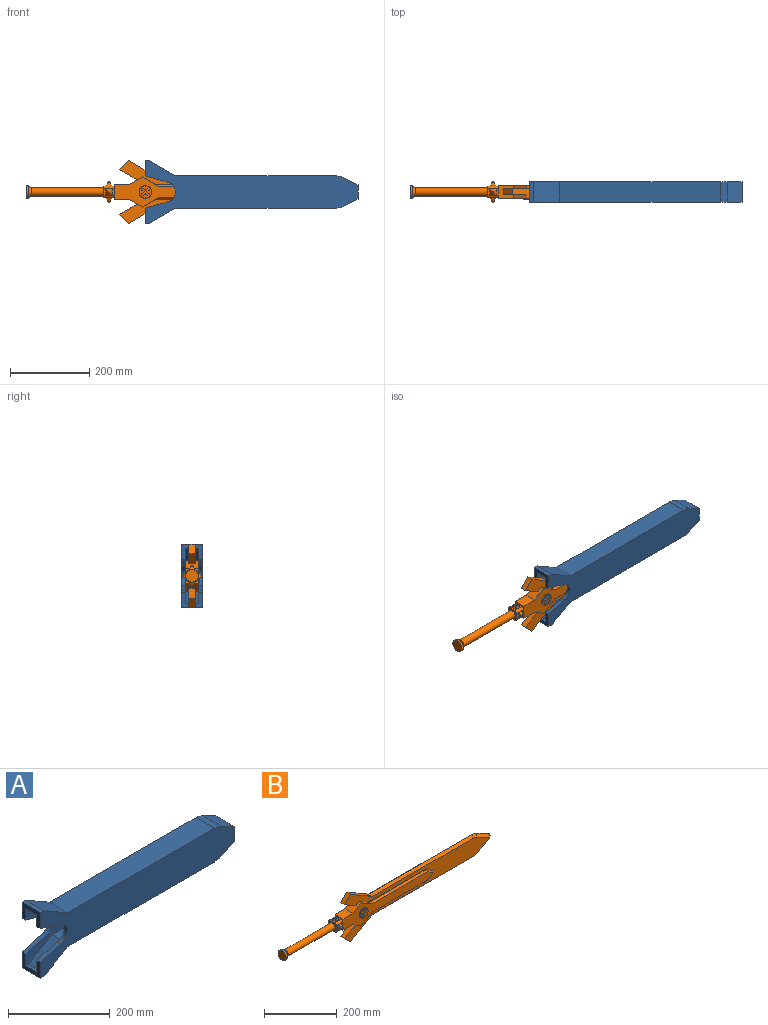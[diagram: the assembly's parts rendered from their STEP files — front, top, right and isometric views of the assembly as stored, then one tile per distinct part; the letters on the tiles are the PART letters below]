
ASSEMBLY  parts=2 mates=1
PART A: 34 faces, bbox 537.1x50.8x157.5 mm
  f0: plane 50.8x38.1mm, normal (-1,0,0), area 1083.9mm2, adj f1,f9,f10,f19,f20,f23,f32,f33
  f1: plane 57.66x16.19mm, normal (-0.27,0,0.96), area 608.5mm2, adj f0,f2,f20,f33
  f2: cylinder r=25.4mm len=48.91mm, axis (0,1,0), area 669.5mm2, adj f1,f3,f20,f33
  f3: plane 57.66x16.19mm, normal (-0.27,0,-0.96), area 608.5mm2, adj f2,f4,f20,f33
  f4: plane 50.8x38.1mm, normal (-1,0,0), area 1083.9mm2, adj f3,f6,f7,f19,f20,f22,f32,f33
  f5: plane 65.99x50.8mm, normal (0.5,0,0.87), area 3871mm2, adj f6,f18,f19,f20
  f6: plane 50.8x10.21mm, normal (0,0,1), area 518.6mm2, adj f4,f5,f19,f20
  f7: plane 57.66x16.19mm, normal (-0.27,0,-0.96), area 608.5mm2, adj f4,f8,f19,f32
  f8: cylinder r=25.4mm len=48.91mm, axis (0,1,0), area 669.5mm2, adj f7,f9,f19,f32
  f9: plane 57.66x16.19mm, normal (-0.27,0,0.96), area 608.5mm2, adj f0,f8,f19,f32
  f10: plane 50.8x10.21mm, normal (0,0,-1), area 518.6mm2, adj f0,f11,f19,f20
  f11: plane 65.99x50.8mm, normal (0.5,0,-0.87), area 3871mm2, adj f10,f12,f19,f20
  f12: plane 406.4x50.8mm, normal (0,0,-1), area 20645.1mm2, adj f11,f13,f19,f20
  f13: cylinder r=40.64mm len=50.8mm, axis (0,1,0), area 957.2mm2, adj f12,f14,f19,f20
  f14: plane 50.8x36.35mm, normal (0.45,0,-0.89), area 2064.5mm2, adj f13,f15,f19,f20
  f15: plane 50.8x36.35mm, normal (1,0,0), area 1846.6mm2, adj f14,f16,f19,f20
  f16: plane 50.8x36.35mm, normal (0.45,0,0.89), area 2064.5mm2, adj f15,f17,f19,f20
  f17: cylinder r=40.64mm len=50.8mm, axis (0,1,0), area 957.2mm2, adj f16,f18,f19,f20
  f18: plane 406.4x50.8mm, normal (0,0,1), area 20645.1mm2, adj f5,f17,f19,f20
  f19: plane 537.12x157.48mm, normal (0,-1,0), area 41503.6mm2, adj f0,f4,f5,f6,f7,f8,f9,f10
  f20: plane 537.12x157.48mm, normal (0,1,0), area 41503.6mm2, adj f0,f1,f2,f3,f4,f5,f6,f10
  f21: plane 65.99x38.1mm, normal (-0.5,0,-0.87), area 2322.6mm2, adj f22,f31,f32,f33
  f22: plane 30.48x7.49mm, normal (0,0,-1), area 228.2mm2, adj f4,f21,f32,f33
  f23: plane 30.48x7.49mm, normal (0,0,1), area 228.2mm2, adj f0,f24,f32,f33
  f24: plane 65.99x38.1mm, normal (-0.5,0,0.87), area 2322.6mm2, adj f23,f25,f32,f33
  f25: plane 409.12x30.48mm, normal (0,0,1), area 12470mm2, adj f24,f26,f32,f33
  f26: cylinder r=30.48mm len=30.48mm, axis (0,1,0), area 430.7mm2, adj f25,f27,f32,f33
  f27: plane 30.73x30.48mm, normal (-0.45,0,0.89), area 1047.3mm2, adj f26,f28,f32,f33
  f28: plane 30.48x23.79mm, normal (-1,0,0), area 725.2mm2, adj f27,f29,f32,f33
  f29: plane 30.73x30.48mm, normal (-0.45,0,-0.89), area 1047.3mm2, adj f28,f30,f32,f33
  f30: cylinder r=30.48mm len=30.48mm, axis (0,1,0), area 430.7mm2, adj f29,f31,f32,f33
  f31: plane 409.12x30.48mm, normal (0,0,-1), area 12470mm2, adj f21,f30,f32,f33
  f32: plane 526.96x137.16mm, normal (0,1,0), area 30087.2mm2, adj f0,f4,f7,f8,f9,f21,f22,f23
  f33: plane 526.96x137.16mm, normal (0,-1,0), area 30087.2mm2, adj f0,f1,f2,f3,f4,f21,f22,f23
PART B: 132 faces, bbox 810.5x54x159.9 mm
  f0: plane 18.57x12.28mm, normal (0,-1,0), area 81.6mm2, adj f80,f81,f82,f105,f106,f107,f108
  f1: plane 18.57x12.28mm, normal (0,-1,0), area 81.6mm2, adj f80,f87,f88,f90,f91,f92,f93
  f2: plane 18.57x12.28mm, normal (0,-1,0), area 81.6mm2, adj f80,f85,f86,f100,f101,f102,f103
  f3: plane 18.57x12.28mm, normal (0,-1,0), area 81.6mm2, adj f80,f83,f84,f95,f96,f97,f98
  f4: plane 10.7x10.7mm, normal (0,0.89,-0.45), area 64mm2, adj f8,f55,f57
  f5: plane 10.7x10.7mm, normal (0,-0.89,-0.45), area 64mm2, adj f8,f53,f54
  f6: plane 10.7x10.7mm, normal (0,-0.45,0.89), area 64mm2, adj f9,f58,f62
  f7: plane 10.7x10.7mm, normal (0,-0.45,-0.89), area 64mm2, adj f9,f59,f60
  f8: plane 25.4x15.88mm, normal (0,0,-1), area 175.1mm2, adj f4,f5,f11,f39,f51,f52,f53,f54
  f9: plane 25.4x15.88mm, normal (0,-1,0), area 175.1mm2, adj f6,f7,f11,f39,f49,f50,f58,f59
  f10: plane 25.4x15.88mm, normal (0,0,1), area 175.1mm2, adj f11,f39,f45,f46,f47,f48,f63,f64
  f11: plane 38.1x30.48mm, normal (-1,0,0), area 312.4mm2, adj f8,f9,f10,f28,f29,f30,f37,f38
  f12: plane 23.24x23.24mm, normal (-0.71,0,-0.71), area 500.9mm2, adj f14,f15,f17,f19
  f13: plane 23.24x23.24mm, normal (-0.71,0,0.71), area 500.9mm2, adj f14,f15,f16,f18
  f14: plane 567.12x159.87mm, normal (0,-1,0), area 23056.7mm2, adj f12,f13,f16,f17,f18,f19,f26,f27
  f15: plane 567.12x159.87mm, normal (0,1,0), area 23056.7mm2, adj f12,f13,f16,f17,f18,f19,f20,f21
  f16: plane 44.91x25.93mm, normal (-0.5,0,-0.87), area 790.2mm2, adj f13,f14,f15,f26
  f17: plane 44.91x25.93mm, normal (-0.5,0,0.87), area 790.2mm2, adj f12,f14,f15,f27
  f18: plane 85.66x49.46mm, normal (0.5,0,0.87), area 1391.3mm2, adj f13,f14,f15,f110,f117
  f19: plane 85.66x49.46mm, normal (0.5,0,-0.87), area 1391.3mm2, adj f12,f14,f15,f116,f123
  f20: plane 41.79x24.13mm, normal (0.5,0,-0.87), area 316.1mm2, adj f15,f21,f27,f30,f124
  f21: plane 228.6x2.54mm, normal (0,0,-1), area 580.6mm2, adj f15,f20,f22,f124
  f22: plane 22.7x19.05mm, normal (0.64,0,-0.77), area 75.3mm2, adj f15,f21,f23,f126
  f23: plane 22.7x19.05mm, normal (0.64,0,0.77), area 75.3mm2, adj f15,f22,f24,f127
  f24: plane 228.6x2.54mm, normal (0,0,1), area 580.6mm2, adj f15,f23,f25,f125
  f25: plane 41.79x24.13mm, normal (0.5,0,0.87), area 316.1mm2, adj f15,f24,f26,f30,f125
  f26: plane 33x30.48mm, normal (-0.5,0,0.87), area 937.8mm2, adj f14,f15,f16,f25,f28,f30,f36,f37
  f27: plane 33x30.48mm, normal (-0.5,0,-0.87), area 937.8mm2, adj f14,f15,f17,f20,f29,f30,f31,f37
  f28: plane 38.1x30.48mm, normal (0,0,1), area 1161.3mm2, adj f11,f26,f30,f37
  f29: plane 38.1x30.48mm, normal (0,0,-1), area 1161.3mm2, adj f11,f27,f30,f37
  f30: plane 347.49x76.2mm, normal (0,1,0), area 11835.7mm2, adj f11,f20,f25,f26,f27,f28,f29,f124
  f31: plane 41.79x24.13mm, normal (0.5,0,-0.87), area 316.1mm2, adj f14,f27,f32,f37,f128
  f32: plane 228.6x2.54mm, normal (0,0,-1), area 580.6mm2, adj f14,f31,f33,f128
  f33: plane 22.7x19.05mm, normal (0.64,0,-0.77), area 75.3mm2, adj f14,f32,f34,f131
  f34: plane 22.7x19.05mm, normal (0.64,0,0.77), area 75.3mm2, adj f14,f33,f35,f130
  f35: plane 228.6x2.54mm, normal (0,0,1), area 580.6mm2, adj f14,f34,f36,f129
  f36: plane 41.79x24.13mm, normal (0.5,0,0.87), area 316.1mm2, adj f14,f26,f35,f37,f129
  f37: plane 347.49x76.2mm, normal (0,-1,0), area 11044mm2, adj f11,f26,f27,f28,f29,f31,f36,f80
  f38: plane 25.4x15.88mm, normal (0,1,0), area 175.1mm2, adj f11,f39,f41,f42,f43,f44,f68,f69
  f39: plane 29.85x29.85mm, normal (-1,0,0), area 524.5mm2, adj f8,f9,f10,f38,f40,f73,f74,f75
  f40: cylinder r=10.16mm len=183.12mm, axis (1,0,0), area 11690mm2, adj f39,f79
  f41: plane 10.7x10.7mm, normal (0.89,0.45,0), area 64mm2, adj f38,f70,f72
  f42: plane 10.7x10.7mm, normal (-0.89,0.45,0), area 64mm2, adj f38,f68,f69
  f43: plane 10.7x10.7mm, normal (0,0.45,-0.89), area 64mm2, adj f38,f69,f70
  f44: plane 10.7x10.7mm, normal (0,0.45,0.89), area 64mm2, adj f38,f68,f72
  f45: plane 10.7x10.7mm, normal (0,0.89,0.45), area 64mm2, adj f10,f63,f67
  f46: plane 10.7x10.7mm, normal (0,-0.89,0.45), area 64mm2, adj f10,f64,f65
  f47: plane 10.7x10.7mm, normal (0.89,0,0.45), area 64mm2, adj f10,f63,f64
  f48: plane 10.7x10.7mm, normal (-0.89,0,0.45), area 64mm2, adj f10,f65,f67
  f49: plane 10.7x10.7mm, normal (0.89,-0.45,0), area 64mm2, adj f9,f58,f59
  f50: plane 10.7x10.7mm, normal (-0.89,-0.45,0), area 64mm2, adj f9,f60,f62
  f51: plane 10.7x10.7mm, normal (0.89,0,-0.45), area 64mm2, adj f8,f54,f55
  f52: plane 10.7x10.7mm, normal (-0.89,0,-0.45), area 64mm2, adj f8,f53,f57
  f53: cylinder r=2.54mm len=11.36mm, axis (0.41,0.41,-0.82), area 46.5mm2, adj f5,f8,f52,f56
  f54: cylinder r=2.54mm len=11.36mm, axis (0.41,-0.41,0.82), area 46.5mm2, adj f5,f8,f51,f56
  f55: cylinder r=2.54mm len=11.36mm, axis (-0.41,-0.41,-0.82), area 46.5mm2, adj f4,f8,f51,f56
  f56: sphere r=2.54mm, area 18.8mm2, adj f53,f54,f55,f57
  f57: cylinder r=2.54mm len=11.36mm, axis (-0.41,0.41,0.82), area 46.5mm2, adj f4,f8,f52,f56
  f58: cylinder r=2.54mm len=11.36mm, axis (0.41,0.82,0.41), area 46.5mm2, adj f6,f9,f49,f61
  f59: cylinder r=2.54mm len=11.36mm, axis (-0.41,-0.82,0.41), area 46.5mm2, adj f7,f9,f49,f61
  f60: cylinder r=2.54mm len=11.36mm, axis (-0.41,0.82,-0.41), area 46.5mm2, adj f7,f9,f50,f61
  f61: sphere r=2.54mm, area 18.8mm2, adj f58,f59,f60,f62
  f62: cylinder r=2.54mm len=11.36mm, axis (0.41,-0.82,-0.41), area 46.5mm2, adj f6,f9,f50,f61
  f63: cylinder r=2.54mm len=11.36mm, axis (0.41,0.41,-0.82), area 46.5mm2, adj f10,f45,f47,f66
  f64: cylinder r=2.54mm len=11.36mm, axis (-0.41,0.41,0.82), area 46.5mm2, adj f10,f46,f47,f66
  f65: cylinder r=2.54mm len=11.36mm, axis (-0.41,-0.41,-0.82), area 46.5mm2, adj f10,f46,f48,f66
  f66: sphere r=2.54mm, area 18.8mm2, adj f63,f64,f65,f67
  f67: cylinder r=2.54mm len=11.36mm, axis (0.41,-0.41,0.82), area 46.5mm2, adj f10,f45,f48,f66
  f68: cylinder r=2.54mm len=11.36mm, axis (0.41,0.82,-0.41), area 46.5mm2, adj f38,f42,f44,f71
  f69: cylinder r=2.54mm len=11.36mm, axis (-0.41,-0.82,-0.41), area 46.5mm2, adj f38,f42,f43,f71
  f70: cylinder r=2.54mm len=11.36mm, axis (-0.41,0.82,0.41), area 46.5mm2, adj f38,f41,f43,f71
  f71: sphere r=2.54mm, area 18.8mm2, adj f68,f69,f70,f72
  f72: cylinder r=2.54mm len=11.36mm, axis (0.41,-0.82,0.41), area 46.5mm2, adj f38,f41,f44,f71
  f73: cylinder r=6.99mm len=25.4mm, axis (1,0,0), area 278.7mm2, adj f10,f11,f38,f39
  f74: cylinder r=6.99mm len=25.4mm, axis (-1,0,0), area 278.7mm2, adj f9,f10,f11,f39
  f75: cylinder r=6.99mm len=25.4mm, axis (1,0,0), area 278.7mm2, adj f8,f9,f11,f39
  f76: cylinder r=6.99mm len=25.4mm, axis (-1,0,0), area 278.7mm2, adj f8,f11,f38,f39
  f77: cylinder r=15.88mm len=31.75mm, axis (1,0,0), area 633.4mm2, adj f78,f79
  f78: plane 31.75x31.75mm, normal (-1,0,0), area 791.7mm2, adj f77
  f79: torus R=17.78mm, axis (-1,0,0), area 768.8mm2, adj f40,f77
  f80: cylinder r=15.88mm len=31.75mm, axis (0,1,0), area 279.3mm2, adj f0,f1,f2,f3,f37,f81,f82,f83
  f81: plane 9.28x9.28mm, normal (-0.71,0,-0.71), area 16.7mm2, adj f0,f80,f82,f89
  f82: plane 9.28x9.28mm, normal (-0.71,0,0.71), area 16.7mm2, adj f0,f80,f81,f89
  f83: plane 9.28x9.28mm, normal (0.71,0,-0.71), area 16.7mm2, adj f3,f80,f84,f89
  f84: plane 9.28x9.28mm, normal (-0.71,0,-0.71), area 16.7mm2, adj f3,f80,f83,f89
  f85: plane 9.28x9.28mm, normal (0.71,0,0.71), area 16.7mm2, adj f2,f80,f86,f89
  f86: plane 9.28x9.28mm, normal (0.71,0,-0.71), area 16.7mm2, adj f2,f80,f85,f89
  f87: plane 9.28x9.28mm, normal (-0.71,0,0.71), area 16.7mm2, adj f1,f80,f88,f89
  f88: plane 9.28x9.28mm, normal (0.71,0,0.71), area 16.7mm2, adj f1,f80,f87,f89
  f89: plane 25.75x25.75mm, normal (0,-1,0), area 295.4mm2, adj f80,f81,f82,f83,f84,f85,f86,f87
  f90: plane 4.61x4.61mm, normal (-0.71,0,-0.71), area 8.3mm2, adj f1,f91,f93,f94
  f91: plane 4.61x4.61mm, normal (0.71,0,-0.71), area 8.3mm2, adj f1,f90,f92,f94
  f92: plane 4.61x4.61mm, normal (0.71,0,0.71), area 8.3mm2, adj f1,f91,f93,f94
  f93: plane 4.61x4.61mm, normal (-0.71,0,0.71), area 8.3mm2, adj f1,f90,f92,f94
  f94: plane 9.22x9.22mm, normal (0,-1,0), area 42.5mm2, adj f90,f91,f92,f93
  f95: plane 4.61x4.61mm, normal (0.71,0,0.71), area 8.3mm2, adj f3,f96,f98,f99
  f96: plane 4.61x4.61mm, normal (-0.71,0,0.71), area 8.3mm2, adj f3,f95,f97,f99
  f97: plane 4.61x4.61mm, normal (-0.71,0,-0.71), area 8.3mm2, adj f3,f96,f98,f99
  f98: plane 4.61x4.61mm, normal (0.71,0,-0.71), area 8.3mm2, adj f3,f95,f97,f99
  f99: plane 9.22x9.22mm, normal (0,-1,0), area 42.5mm2, adj f95,f96,f97,f98
  f100: plane 4.61x4.61mm, normal (-0.71,0,0.71), area 8.3mm2, adj f2,f101,f103,f104
  f101: plane 4.61x4.61mm, normal (-0.71,0,-0.71), area 8.3mm2, adj f2,f100,f102,f104
  f102: plane 4.61x4.61mm, normal (0.71,0,-0.71), area 8.3mm2, adj f2,f101,f103,f104
  f103: plane 4.61x4.61mm, normal (0.71,0,0.71), area 8.3mm2, adj f2,f100,f102,f104
  f104: plane 9.22x9.22mm, normal (0,-1,0), area 42.5mm2, adj f100,f101,f102,f103
  f105: plane 4.61x4.61mm, normal (0.71,0,0.71), area 8.3mm2, adj f0,f106,f108,f109
  f106: plane 4.61x4.61mm, normal (-0.71,0,0.71), area 8.3mm2, adj f0,f105,f107,f109
  f107: plane 4.61x4.61mm, normal (-0.71,0,-0.71), area 8.3mm2, adj f0,f106,f108,f109
  f108: plane 4.61x4.61mm, normal (0.71,0,-0.71), area 8.3mm2, adj f0,f105,f107,f109
  f109: plane 9.22x9.22mm, normal (0,-1,0), area 42.5mm2, adj f105,f106,f107,f108
  f110: plane 406.4x7.62mm, normal (0,-0.71,0.71), area 4308.4mm2, adj f14,f18,f111,f117
  f111: cone r=30.48mm half-angle=45deg, axis (0,1,0), area 171.3mm2, adj f14,f110,f112,f118
  f112: plane 53.39x31.81mm, normal (0.32,-0.71,0.63), area 602.2mm2, adj f14,f111,f113,f119
  f113: cone r=2.54mm half-angle=45deg, axis (0,1,0), area 151.5mm2, adj f14,f112,f114,f120
  f114: plane 53.39x31.81mm, normal (0.32,-0.71,-0.63), area 602.2mm2, adj f14,f113,f115,f121
  f115: cone r=30.48mm half-angle=45deg, axis (0,1,0), area 171.3mm2, adj f14,f114,f116,f122
  f116: plane 406.4x7.62mm, normal (0,-0.71,-0.71), area 4308.4mm2, adj f14,f19,f115,f123
  f117: plane 406.4x7.62mm, normal (0,0.71,0.71), area 4308.4mm2, adj f15,f18,f110,f118
  f118: cone r=38.1mm half-angle=45deg, axis (0,-1,0), area 171.3mm2, adj f15,f111,f117,f119
  f119: plane 53.39x31.81mm, normal (0.32,0.71,0.63), area 602.2mm2, adj f15,f112,f118,f120
  f120: cone r=2.54mm half-angle=45deg, axis (0,-1,0), area 151.5mm2, adj f15,f113,f119,f121
  f121: plane 53.39x31.81mm, normal (0.32,0.71,-0.63), area 602.2mm2, adj f15,f114,f120,f122
  f122: cone r=38.1mm half-angle=45deg, axis (0,-1,0), area 171.3mm2, adj f15,f115,f121,f123
  f123: plane 406.4x7.62mm, normal (0,0.71,-0.71), area 4308.4mm2, adj f15,f19,f116,f122
  f124: plane 228.6x5.08mm, normal (0,0.71,-0.71), area 1604.1mm2, adj f20,f21,f30,f126
  f125: plane 228.6x5.08mm, normal (0,0.71,0.71), area 1604.1mm2, adj f24,f25,f30,f127
  f126: plane 24.55x19.05mm, normal (0.45,0.71,-0.54), area 184.5mm2, adj f22,f30,f124,f127
  f127: plane 24.55x19.05mm, normal (0.45,0.71,0.54), area 184.5mm2, adj f23,f30,f125,f126
  f128: plane 228.6x5.08mm, normal (0,-0.71,-0.71), area 1604.1mm2, adj f31,f32,f37,f131
  f129: plane 228.6x5.08mm, normal (0,-0.71,0.71), area 1604.1mm2, adj f35,f36,f37,f130
  f130: plane 24.55x19.05mm, normal (0.45,-0.71,0.54), area 184.5mm2, adj f34,f37,f129,f131
  f131: plane 24.55x19.05mm, normal (0.45,-0.71,-0.54), area 184.5mm2, adj f33,f37,f128,f130
PLACE A t=(274.45,-13.65,-13.1)mm fixed
PLACE B t=(228.5,-13.65,-13.1)mm
MATE slider B.f77 <-> A.f28  axis (-1,0,0) through (-509.35,-13.65,-13.1)mm
